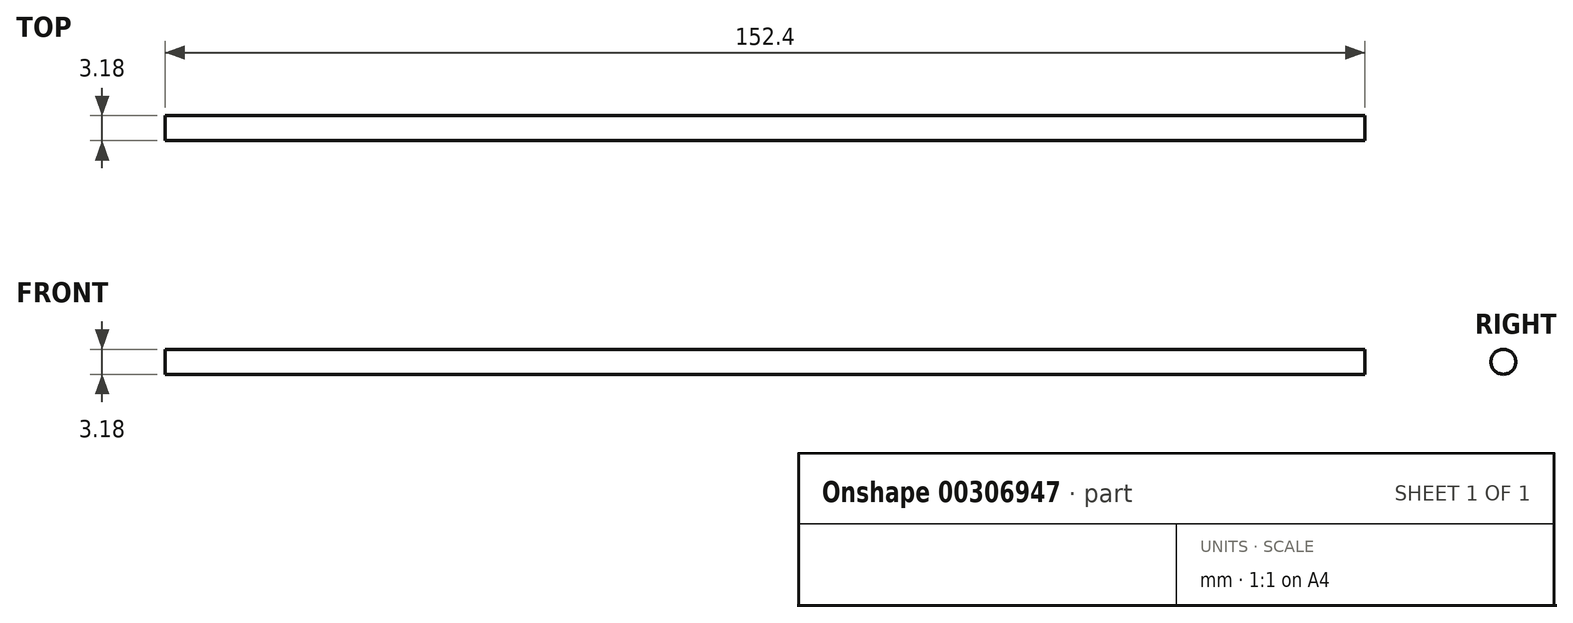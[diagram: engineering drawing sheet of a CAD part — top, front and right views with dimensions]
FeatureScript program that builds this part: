
annotation { "Feature Type Name" : "Feature", "Feature Type Description" : "" }
export const myFeature = defineFeature(function(context is Context, id is Id, definition is map)
    precondition{}
    {
        {
            var Q0;
            Q0=qCreatedBy(makeId("Right.planeOp"),FACE);
            var sketch = newSketch(context, id + "F0", { "sketchPlane" : qUnion([Q0])});
            skCircle(sketch, "E0", {"center": v(0, 0) * mm, "radius": 1.59 * mm});
            skSolve(sketch);
        }
        {
            var Q0;
            Q0=makeQuery(id+"F0.imprint","IMPRINT",FACE,{"disambiguationData":[TD([[makeQuery(id+"F0.imprint","IMPRINT",EDGE,{"derivedFrom":sQuery(id+"F0.wireOp",EDGE,"E0")}),1.0]])]});
            extrude(context, id + "F1", {"entities" : qUnion([Q0]), "oppositeDirection" : true, "depth" : 152.4 * mm});
        }
    });
